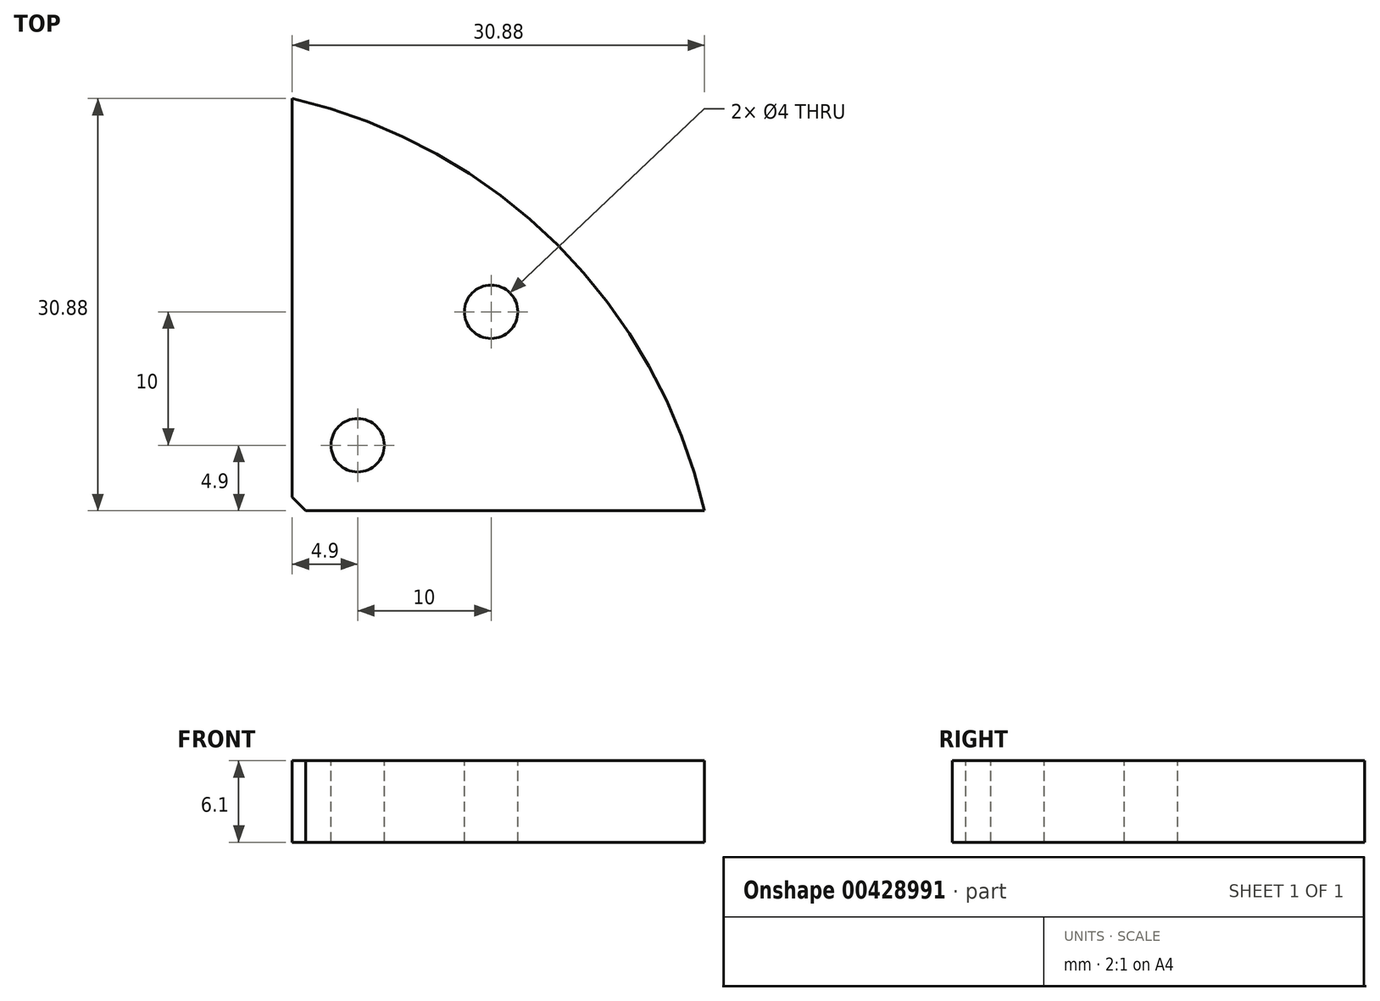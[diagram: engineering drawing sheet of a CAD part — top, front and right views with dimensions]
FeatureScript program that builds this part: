
annotation { "Feature Type Name" : "Feature", "Feature Type Description" : "" }
export const myFeature = defineFeature(function(context is Context, id is Id, definition is map)
    precondition{}
    {
        {
            var Q0;
            Q0=qCreatedBy(makeId("Top.planeOp"),FACE);
            var sketch = newSketch(context, id + "F0", { "sketchPlane" : qUnion([Q0])});
            skArc(sketch, "E0", {"start": v(39.98, 9.1) * mm, "mid": v(29, 29) * mm, "end": v(9.1, 39.98) * mm});
            skLineSegment(sketch, "E1", {"start": v(9.1, 9.1) * mm, "end": v(9.1, 39.98) * mm});
            skLineSegment(sketch, "E2", {"start": v(9.1, 9.1) * mm, "end": v(39.98, 9.1) * mm});
            skSolve(sketch);
        }
        {
            var Q0;
            Q0=qSketchRegion(id+"F0",true);
            extrude(context, id + "F1", {"entities" : qUnion([Q0]), "depth" : 6.1 * mm});
        }
        {
            var Q0;
            Q0=makeQuery(id+"F1.opExtrude","CAP_FACE",FACE,{"disambiguationData":[OSD([sQuery(id+"F0.wireOp",EDGE,"E0")])],"isStart":false});
            var sketch = newSketch(context, id + "F2", { "sketchPlane" : qUnion([Q0])});
            skLineSegment(sketch, "E3", {"start": v(0, 0) * mm, "end": v(33.6, 33.6) * mm, "construction": true});
            skCircle(sketch, "E4", {"center": v(14, 14) * mm, "radius": 2 * mm});
            skCircle(sketch, "E5", {"center": v(24, 24) * mm, "radius": 2 * mm});
            skSolve(sketch);
        }
        {
            var Q0;
            Q0=sQuery(id+"F2.wireOp",VERTEX,"E4.center");
            var Q1;
            Q1=sQuery(id+"F2.wireOp",VERTEX,"E5.center");
            var Q2;
            Q2=makeQuery(id+"F1.opExtrude","SWEPT_BODY",BODY,{"disambiguationData":[OSD([sQuery(id+"F0.wireOp",EDGE,"E0")])]});
            hole(context, id + "F3", {"style" : HoleStyle.SIMPLE, "endStyle" : HoleEndStyle.THROUGH, "holeDiameter" : 4 * mm, "isTappedThrough" : true, "tappedDepth" : 12 * mm, "tapClearance" : 3, "startFromSketch" : true, "locations" : qUnion([Q0, Q1]), "scope" : qUnion([Q2])});
        }
        {
            var Q0;
            Q0=makeQuery(id+"F1.opExtrude","SWEPT_EDGE",EDGE,{"disambiguationData":[OSD([sQuery(id+"F0.wireOp",EDGE,"E1"),sQuery(id+"F0.wireOp",EDGE,"E2")])]});
            chamfer(context, id + "F4", {"entities" : qUnion([Q0]), "width" : 1 * mm, "tangentPropagation" : true});
        }
    });
